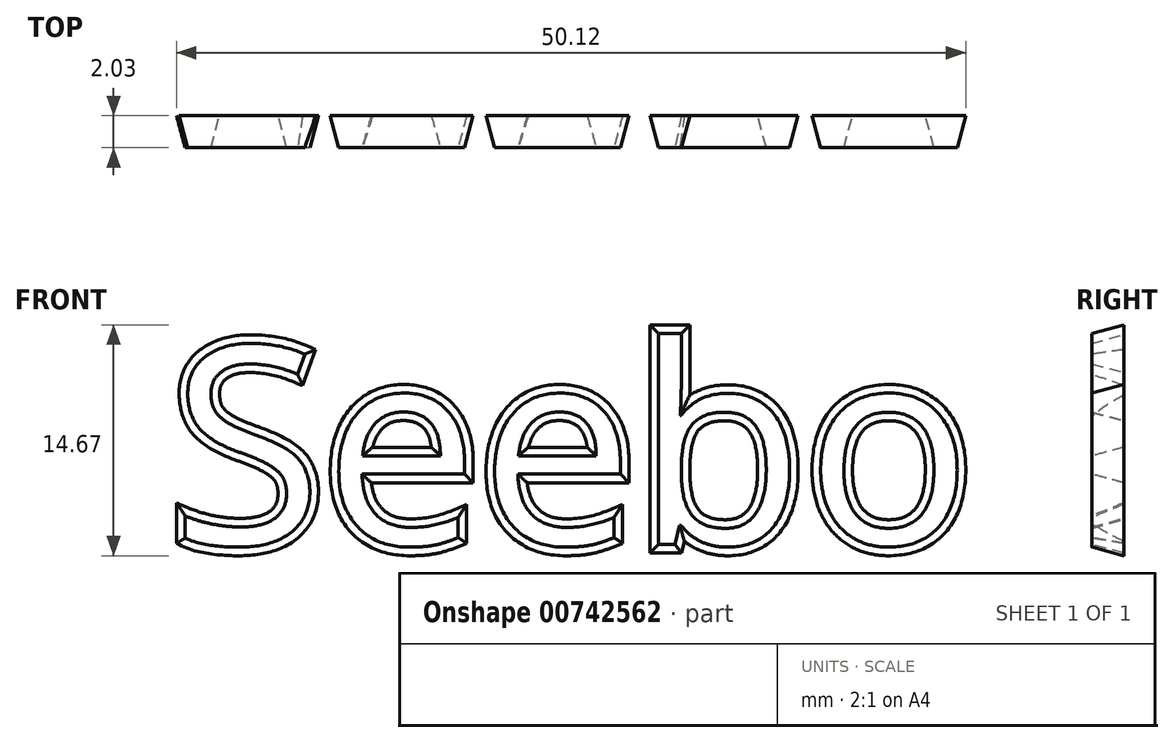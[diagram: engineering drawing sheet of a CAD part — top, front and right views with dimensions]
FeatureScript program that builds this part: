
annotation { "Feature Type Name" : "Feature", "Feature Type Description" : "" }
export const myFeature = defineFeature(function(context is Context, id is Id, definition is map)
    precondition{}
    {
        {
            var Q0;
            Q0=qCreatedBy(makeId("Front.planeOp"),FACE);
            var sketch = newSketch(context, id + "F0", { "sketchPlane" : qUnion([Q0])});
            skLineSegment(sketch, "E0.bottom", {"start": v(-25.4, 15.88) * mm, "end": v(25.4, 15.88) * mm});
            skLineSegment(sketch, "E0.top", {"start": v(-25.4, -15.88) * mm, "end": v(25.4, -15.88) * mm});
            skLineSegment(sketch, "E0.left", {"start": v(-25.4, 15.88) * mm, "end": v(-25.4, -15.88) * mm});
            skLineSegment(sketch, "E0.right", {"start": v(25.4, 15.87) * mm, "end": v(25.4, -15.88) * mm});
            skPoint(sketch, "E0.middle", {"position": v(0, 0) * mm});
            skSolve(sketch);
        }
        {
            var Q0;
            Q0=qCreatedBy(makeId("Front.planeOp"),FACE);
            var sketch = newSketch(context, id + "F1", { "sketchPlane" : qUnion([Q0])});
            skText(sketch, "E1", { "text": "Seebo", "fontName": "OpenSans-Regular.ttf"});
            const initialGuessF1  = {"E1": [-0.02555, -0.00635, 1, 0, 0.0127]};
            skSetInitialGuess(sketch, initialGuessF1);
            skSolve(sketch);
        }
        {
            var Q0;
            Q0=qSketchRegion(id+"F1",true);
            extrude(context, id + "F2", {"entities" : qUnion([Q0]), "oppositeDirection" : true, "depth" : 2.03 * mm, "offsetDistance" : 25.4 * mm, "hasDraft" : true, "draftAngle" : 15 * degree});
        }
    });
